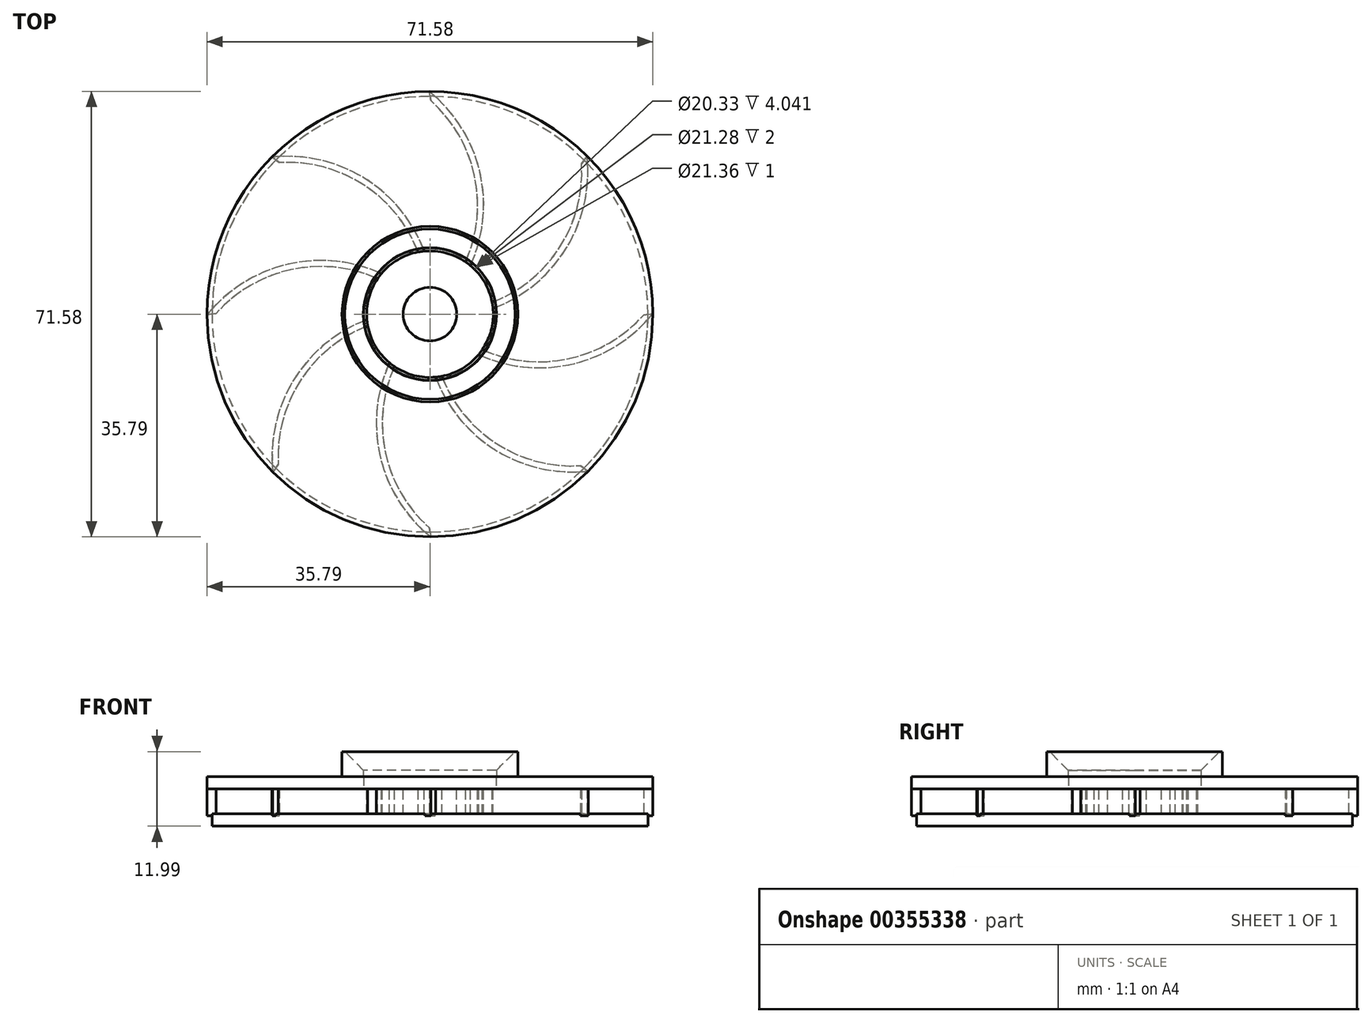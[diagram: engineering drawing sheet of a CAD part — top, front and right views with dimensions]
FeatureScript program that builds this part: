
annotation { "Feature Type Name" : "Feature", "Feature Type Description" : "" }
export const myFeature = defineFeature(function(context is Context, id is Id, definition is map)
    precondition{}
    {
        {
            var Q0;
            Q0=qCreatedBy(makeId("Top.planeOp"),FACE);
            var sketch = newSketch(context, id + "F0", { "sketchPlane" : qUnion([Q0])});
            skCircle(sketch, "E0", {"center": v(0, 0) * mm, "radius": 35 * mm});
            skSolve(sketch);
        }
        {
            var Q0;
            Q0 = qSketchRegion(id + "F0", true);
            extrude(context, id + "F1", {"entities" : qUnion([Q0]), "depth" : 2 * mm});
        }
        {
            var Q0;
            Q0=makeQuery(id+"F1.opExtrude","CAP_FACE",FACE,{"disambiguationData":[OSD([sQuery(id+"F0.wireOp",EDGE,"E0")])],"isStart":false});
            var sketch = newSketch(context, id + "F2", { "sketchPlane" : qUnion([Q0])});
            skCircle(sketch, "E1", {"center": v(0, 0) * mm, "radius": 5 * mm});
            skSolve(sketch);
        }
        {
            var Q0;
            Q0=makeQuery(id+"F2.imprint","IMPRINT",FACE,{"disambiguationData":[TD([[makeQuery(id+"F2.imprint","IMPRINT",EDGE,{"derivedFrom":sQuery(id+"F2.wireOp",EDGE,"E1")}),1.0]])]});
            var Q1;
            Q1=sQuery(id+"F2.wireOp",EDGE,"E1");
            extrude(context, id + "F3", {"entities" : qUnion([Q0]), "surfaceEntities" : qUnion([Q1]), "depth" : 4 * mm});
        }
        {
            var Q0;
            Q0=qCreatedBy(makeId("Front.planeOp"),FACE);
            var sketch = newSketch(context, id + "F4", { "sketchPlane" : qUnion([Q0])});
            skLineSegment(sketch, "E2.bottom", {"start": v(0.75, 9.72) * mm, "end": v(-0.75, 9.72) * mm});
            skLineSegment(sketch, "E2.top", {"start": v(0.75, 1.7) * mm, "end": v(-0.75, 1.7) * mm});
            skLineSegment(sketch, "E2.left", {"start": v(0.75, 9.72) * mm, "end": v(0.75, 1.7) * mm});
            skLineSegment(sketch, "E2.right", {"start": v(-0.75, 9.72) * mm, "end": v(-0.75, 1.7) * mm});
            skSolve(sketch);
        }
        {
            var Q0;
            Q0=qCreatedBy(makeId("Top.planeOp"),FACE);
            var sketch = newSketch(context, id + "F5", { "sketchPlane" : qUnion([Q0])});
            skArc(sketch, "E3", {"start": v(0, 0) * mm, "mid": v(-8.13, -17.53) * mm, "end": v(0, -35.05) * mm});
            skSolve(sketch);
        }
        {
            var Q0;
            Q0 = qSketchRegion(id + "F4", true);
            var Q1;
            Q1=sQuery(id+"F5.wireOp",EDGE,"E3");
            sweep(context, id + "F6", {"profiles" : qUnion([Q0]), "path" : qUnion([Q1])});
        }
        {
            var Q0;
            Q0=makeQuery(id+"F6.opSweep","SWEPT_BODY",BODY,{"disambiguationData":[OSD([sQuery(id+"F4.wireOp",EDGE,"E2.bottom"),sQuery(id+"F4.wireOp",EDGE,"E2.top"),sQuery(id+"F4.wireOp",EDGE,"E2.left"),sQuery(id+"F4.wireOp",EDGE,"E2.right"),sQuery(id+"F5.wireOp",EDGE,"E3")])]});
            var Q1;
            Q1=makeQuery(id+"F3.opExtrude","CAP_EDGE",EDGE,{"disambiguationData":[OSD([sQuery(id+"F2.wireOp",EDGE,"E1")])],"isStart":false});
            circularPattern(context, id + "F7", {"operationType" : NewBodyOperationType.ADD, "entities" : qUnion([Q0]), "axis" : qUnion([Q1]), "angle" : 360 * degree, "instanceCount" : 8, "equalSpace" : true});
        }
        {
            var Q0;
            Q0=qCreatedBy(makeId("Front.planeOp"),FACE);
            var sketch = newSketch(context, id + "F8", { "sketchPlane" : qUnion([Q0])});
            skLineSegment(sketch, "E4.bottom", {"start": v(10.16, 13.63) * mm, "end": v(36.83, 13.63) * mm});
            skLineSegment(sketch, "E4.top", {"start": v(10.16, 6) * mm, "end": v(36.83, 6) * mm});
            skLineSegment(sketch, "E4.left", {"start": v(10.16, 13.63) * mm, "end": v(10.16, 6) * mm});
            skLineSegment(sketch, "E4.right", {"start": v(36.83, 13.63) * mm, "end": v(36.83, 6) * mm});
            skLineSegment(sketch, "E5.bottom", {"start": v(10.16, 13.63) * mm, "end": v(4.3, 13.63) * mm});
            skLineSegment(sketch, "E5.top", {"start": v(10.16, 1.95) * mm, "end": v(4.3, 1.95) * mm});
            skLineSegment(sketch, "E5.left", {"start": v(10.16, 13.63) * mm, "end": v(10.16, 1.95) * mm});
            skLineSegment(sketch, "E5.right", {"start": v(4.3, 13.63) * mm, "end": v(4.3, 1.95) * mm});
            skSolve(sketch);
        }
        {
            var Q0;
            Q0 = qSketchRegion(id + "F8", true);
            var Q1;
            Q1=makeQuery(id+"F1.opExtrude","CAP_EDGE",EDGE,{"disambiguationData":[OSD([sQuery(id+"F0.wireOp",EDGE,"E0")])],"isStart":true});
            revolve(context, id + "F9", {"operationType" : NewBodyOperationType.REMOVE, "entities" : qUnion([Q0]), "axis" : qUnion([Q1]), "revolveType" : RevolveType.FULL, "oppositeDirection" : true});
        }
        {
            var Q0;
            {var subQ1=sQuery(id+"F4.wireOp",EDGE,"E2.left");var subQ2=sQuery(id+"F5.wireOp",EDGE,"E3");Q0=makeQuery(id+"F9.boolean.opBoolean","COPY",FACE,{"disambiguationData":[TD([makeQuery(id+"F7.opPattern","COPY",FACE,{"derivedFrom":makeQuery(id+"F6.opSweep","SWEPT_FACE",FACE,{"disambiguationData":[OSD([subQ1,subQ2])]}),"instanceName":"1"})])],"derivedFrom":makeQuery(id+"F9.opRevolve","SWEPT_FACE",FACE,{"disambiguationData":[OSD([sQuery(id+"F8.wireOp",EDGE,"E4.top")])]})});}
            var sketch = newSketch(context, id + "F10", { "sketchPlane" : qUnion([Q0])});
            skCircle(sketch, "E6", {"center": v(0, 0) * mm, "radius": 10.64 * mm});
            skCircle(sketch, "E7", {"center": v(0, 0) * mm, "radius": 35.8 * mm});
            skSolve(sketch);
        }
        {
            var Q0;
            Q0 = qSketchRegion(id + "F10", true);
            extrude(context, id + "F11", {"entities" : qUnion([Q0]), "operationType" : NewBodyOperationType.ADD, "depth" : 2 * mm});
        }
        {
            var Q0;
            {var subQ0=sQuery(id+"F2.wireOp",EDGE,"E1");var subQ1=sQuery(id+"F5.wireOp",EDGE,"E3");Q0=makeQuery(id+"F7.boolean.opBoolean","SPLIT",FACE,{"disambiguationData":[TD([makeQuery(id+"F6.opSweep","SWEPT_FACE",FACE,{"disambiguationData":[OSD([sQuery(id+"F4.wireOp",EDGE,"E2.right"),subQ1])]})])],"derivedFrom":makeQuery(id+"F3.opExtrude","CAP_FACE",FACE,{"disambiguationData":[OSD([subQ0])],"isStart":false})});}
            var sketch = newSketch(context, id + "F12", { "sketchPlane" : qUnion([Q0])});
            skCircle(sketch, "E8", {"center": v(0, 0) * mm, "radius": 7.89 * mm});
            skSolve(sketch);
        }
        {
            var Q0;
            Q0=makeQuery(id+"F12.imprint","IMPRINT",FACE,{"disambiguationData":[TD([[makeQuery(id+"F12.imprint","IMPRINT",EDGE,{"derivedFrom":sQuery(id+"F12.wireOp",EDGE,"E8")}),1.0]])]});
            extrude(context, id + "F13", {"entities" : qUnion([Q0]), "operationType" : NewBodyOperationType.REMOVE, "depth" : 25 * mm});
        }
        {
            var Q0;
            Q0=makeQuery(id+"F11.opExtrude","CAP_FACE",FACE,{"disambiguationData":[OSD([sQuery(id+"F10.wireOp",EDGE,"E6"),sQuery(id+"F10.wireOp",EDGE,"E7")])],"isStart":false});
            var sketch = newSketch(context, id + "F14", { "sketchPlane" : qUnion([Q0])});
            skCircle(sketch, "E9", {"center": v(0, 0) * mm, "radius": 14.11 * mm});
            skCircle(sketch, "E10", {"center": v(0, 0) * mm, "radius": 10.68 * mm});
            skSolve(sketch);
        }
        {
            var Q0;
            Q0 = qSketchRegion(id + "F14", true);
            extrude(context, id + "F15", {"entities" : qUnion([Q0]), "operationType" : NewBodyOperationType.ADD, "depth" : 4 * mm});
        }
        {
            var Q0;
            Q0=makeQuery(id+"F15.opExtrude","CAP_EDGE",EDGE,{"disambiguationData":[OSD([sQuery(id+"F14.wireOp",EDGE,"E10")])],"isStart":false});
            chamfer(context, id + "F16", {"entities" : qUnion([Q0]), "width" : 3 * mm, "tangentPropagation" : true});
        }
    });
